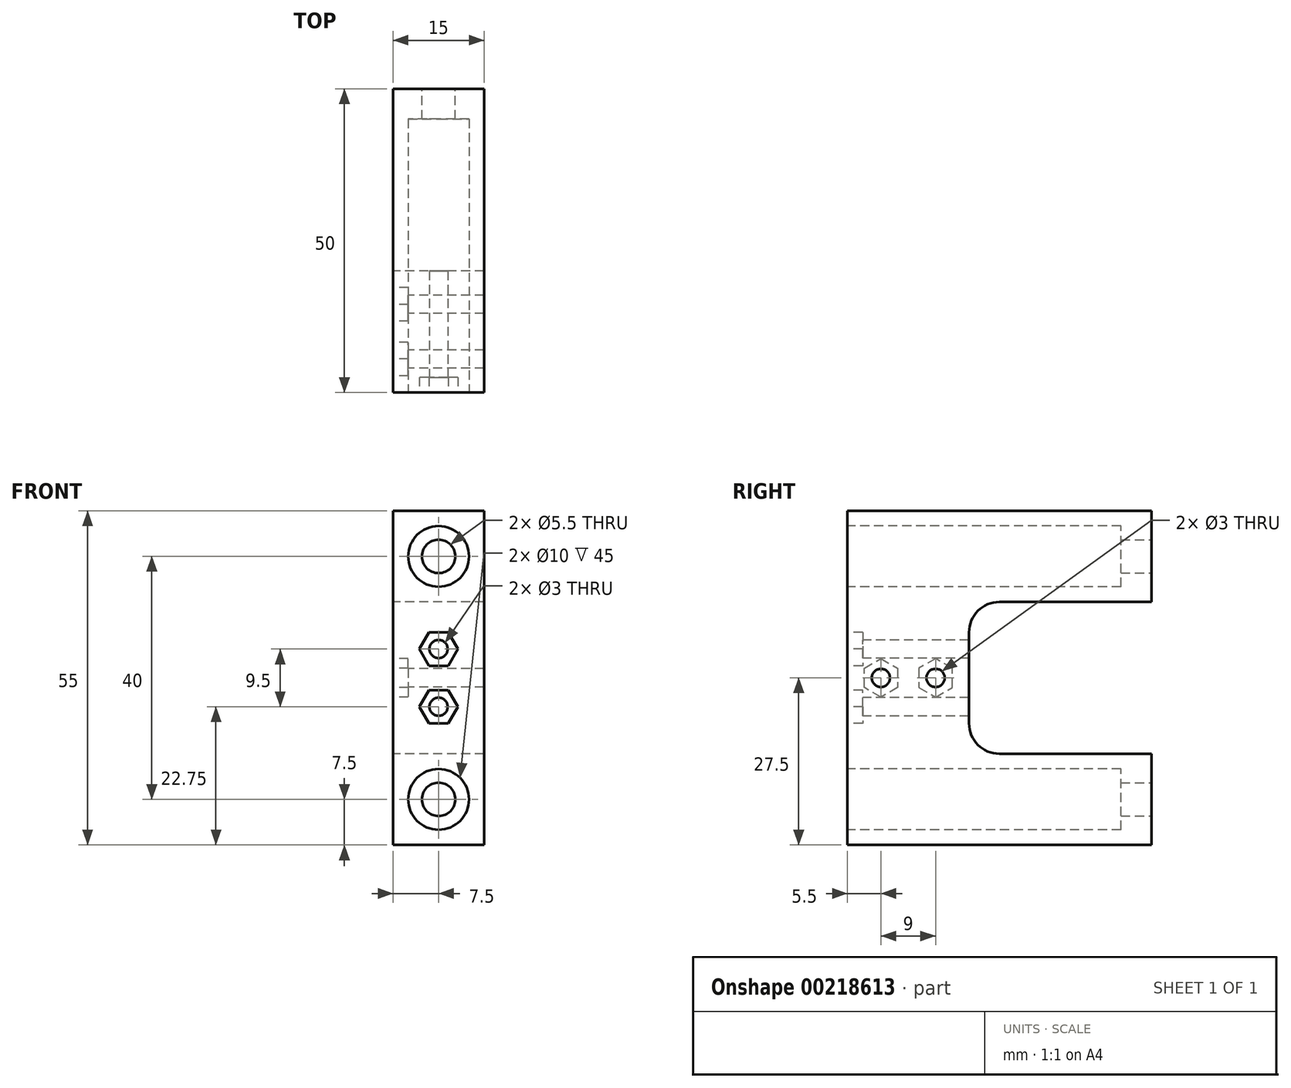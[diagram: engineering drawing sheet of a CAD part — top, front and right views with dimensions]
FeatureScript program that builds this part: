
annotation { "Feature Type Name" : "Feature", "Feature Type Description" : "" }
export const myFeature = defineFeature(function(context is Context, id is Id, definition is map)
    precondition{}
    {
        {
            var Q0;
            Q0=qCreatedBy(makeId("Front.planeOp"),FACE);
            var sketch = newSketch(context, id + "F0", { "sketchPlane" : qUnion([Q0])});
            skLineSegment(sketch, "E0.bottom", {"start": v(7.5, 12.5) * mm, "end": v(-7.5, 12.5) * mm});
            skLineSegment(sketch, "E0.top", {"start": v(7.5, 27.5) * mm, "end": v(-7.5, 27.5) * mm});
            skLineSegment(sketch, "E0.left", {"start": v(7.5, 12.5) * mm, "end": v(7.5, 27.5) * mm});
            skLineSegment(sketch, "E0.right", {"start": v(-7.5, 12.5) * mm, "end": v(-7.5, 27.5) * mm});
            skPoint(sketch, "E0.middle", {"position": v(0, 20) * mm});
            skLineSegment(sketch, "E1", {"start": v(0, 0) * mm, "end": v(34.52, 0) * mm, "construction": true});
            skLineSegment(sketch, "E2.MirrorCS", {"start": v(7.5, -12.5) * mm, "end": v(-7.5, -12.5) * mm});
            skLineSegment(sketch, "E3.MirrorCS", {"start": v(7.5, -12.5) * mm, "end": v(7.5, -27.5) * mm});
            skLineSegment(sketch, "E4.MirrorCS", {"start": v(-7.5, -12.5) * mm, "end": v(-7.5, -27.5) * mm});
            skLineSegment(sketch, "E5.MirrorCS", {"start": v(7.5, -27.5) * mm, "end": v(-7.5, -27.5) * mm});
            skSolve(sketch);
        }
        {
            var Q0;
            Q0 = qSketchRegion(id + "F0", true);
            extrude(context, id + "F1", {"entities" : qUnion([Q0]), "depth" : 50 * mm, "offsetDistance" : 25 * mm});
        }
        {
            var Q0;
            Q0=makeQuery(id+"F1.opExtrude","CAP_FACE",FACE,{"disambiguationData":[OSD([sQuery(id+"F0.wireOp",EDGE,"E0.bottom"),sQuery(id+"F0.wireOp",EDGE,"E0.top"),sQuery(id+"F0.wireOp",EDGE,"E0.left"),sQuery(id+"F0.wireOp",EDGE,"E0.right")])],"isStart":false});
            var sketch = newSketch(context, id + "F2", { "sketchPlane" : qUnion([Q0])});
            skLineSegment(sketch, "E6.bottom", {"start": v(-7.5, 27.5) * mm, "end": v(7.5, 27.5) * mm});
            skLineSegment(sketch, "E6.top", {"start": v(-7.5, -27.5) * mm, "end": v(7.5, -27.5) * mm});
            skLineSegment(sketch, "E6.left", {"start": v(-7.5, 27.5) * mm, "end": v(-7.5, -27.5) * mm});
            skLineSegment(sketch, "E6.right", {"start": v(7.5, 27.5) * mm, "end": v(7.5, -27.5) * mm});
            skSolve(sketch);
        }
        {
            var Q0;
            Q0 = qSketchRegion(id + "F2", true);
            extrude(context, id + "F3", {"entities" : qUnion([Q0]), "operationType" : NewBodyOperationType.ADD, "oppositeDirection" : true, "depth" : 20 * mm, "offsetDistance" : 25 * mm});
        }
        {
            var Q0;
            Q0=makeQuery(id+"F1.opExtrude","CAP_FACE",FACE,{"disambiguationData":[OSD([sQuery(id+"F0.wireOp",EDGE,"E0.bottom"),sQuery(id+"F0.wireOp",EDGE,"E0.top"),sQuery(id+"F0.wireOp",EDGE,"E0.left"),sQuery(id+"F0.wireOp",EDGE,"E0.right")])],"isStart":true});
            var sketch = newSketch(context, id + "F4", { "sketchPlane" : qUnion([Q0])});
            skCircle(sketch, "E7", {"center": v(0, 20) * mm, "radius": 2.75 * mm});
            skPoint(sketch, "E7.centerSnap0", {"position": v(-7.5, 20) * mm});
            skLineSegment(sketch, "E8", {"start": v(0, 0) * mm, "end": v(41.2, 0) * mm, "construction": true});
            skCircle(sketch, "E9.MirrorC", {"center": v(0, -20) * mm, "radius": 2.75 * mm});
            skSolve(sketch);
        }
        {
            var Q0;
            Q0 = qSketchRegion(id + "F4", true);
            extrude(context, id + "F5", {"entities" : qUnion([Q0]), "operationType" : NewBodyOperationType.REMOVE, "endBound" : BoundingType.THROUGH_ALL, "oppositeDirection" : true, "depth" : 25 * mm, "offsetDistance" : 25 * mm});
        }
        {
            var Q0;
            Q0=makeQuery(id+"F3.boolean.opBoolean","MERGE",FACE,{"derivedFrom":[makeQuery(id+"F1.opExtrude","CAP_FACE",FACE,{"disambiguationData":[OSD([sQuery(id+"F0.wireOp",EDGE,"E0.bottom"),sQuery(id+"F0.wireOp",EDGE,"E0.top"),sQuery(id+"F0.wireOp",EDGE,"E0.left"),sQuery(id+"F0.wireOp",EDGE,"E0.right")])],"isStart":false}),makeQuery(id+"F1.opExtrude","CAP_FACE",FACE,{"disambiguationData":[OSD([sQuery(id+"F0.wireOp",EDGE,"E2.MirrorCS"),sQuery(id+"F0.wireOp",EDGE,"E3.MirrorCS"),sQuery(id+"F0.wireOp",EDGE,"E4.MirrorCS"),sQuery(id+"F0.wireOp",EDGE,"E5.MirrorCS")])],"isStart":false}),makeQuery(id+"F3.opExtrude","CAP_FACE",FACE,{"disambiguationData":[OSD([sQuery(id+"F2.wireOp",EDGE,"E6.bottom"),sQuery(id+"F2.wireOp",EDGE,"E6.top"),sQuery(id+"F2.wireOp",EDGE,"E6.left"),sQuery(id+"F2.wireOp",EDGE,"E6.right")])],"isStart":true})]});
            var sketch = newSketch(context, id + "F6", { "sketchPlane" : qUnion([Q0])});
            skCircle(sketch, "E10", {"center": v(0, 20) * mm, "radius": 5 * mm});
            skCircle(sketch, "E11", {"center": v(0, -20) * mm, "radius": 5 * mm});
            skSolve(sketch);
        }
        {
            var Q0;
            Q0 = qSketchRegion(id + "F6", true);
            extrude(context, id + "F7", {"entities" : qUnion([Q0]), "operationType" : NewBodyOperationType.REMOVE, "oppositeDirection" : true, "depth" : 45 * mm, "offsetDistance" : 25 * mm});
        }
        {
            var Q0;
            Q0=makeQuery(id+"F3.boolean.opBoolean","MERGE",FACE,{"derivedFrom":[makeQuery(id+"F1.opExtrude","SWEPT_FACE",FACE,{"disambiguationData":[OSD([sQuery(id+"F0.wireOp",EDGE,"E0.right")])]}),makeQuery(id+"F1.opExtrude","SWEPT_FACE",FACE,{"disambiguationData":[OSD([sQuery(id+"F0.wireOp",EDGE,"E4.MirrorCS")])]}),makeQuery(id+"F3.opExtrude","SWEPT_FACE",FACE,{"disambiguationData":[OSD([sQuery(id+"F2.wireOp",EDGE,"E6.left")])]})]});
            var sketch = newSketch(context, id + "F8", { "sketchPlane" : qUnion([Q0])});
            skCircle(sketch, "E12.cCircle", {"center": v(35.5, 0) * mm, "radius": 2.75 * mm, "construction": true});
            skLineSegment(sketch, "E12.0", {"start": v(38.25, -1.59) * mm, "end": v(35.5, -3.18) * mm});
            skLineSegment(sketch, "E12.1", {"start": v(35.5, -3.18) * mm, "end": v(32.75, -1.59) * mm});
            skLineSegment(sketch, "E12.2", {"start": v(32.75, -1.59) * mm, "end": v(32.75, 1.59) * mm});
            skLineSegment(sketch, "E12.3", {"start": v(32.75, 1.59) * mm, "end": v(35.5, 3.18) * mm});
            skLineSegment(sketch, "E12.4", {"start": v(35.5, 3.18) * mm, "end": v(38.25, 1.59) * mm});
            skLineSegment(sketch, "E12.5", {"start": v(38.25, 1.59) * mm, "end": v(38.25, -1.59) * mm});
            skPoint(sketch, "E12.0.midPoint", {"position": v(36.88, -2.38) * mm});
            skLineSegment(sketch, "E13", {"start": v(30, 0) * mm, "end": v(50, 0) * mm, "construction": true});
            skLineSegment(sketch, "E14", {"start": v(40, 0) * mm, "end": v(40, 5.04) * mm, "construction": true});
            skCircle(sketch, "E15.MirrorC", {"center": v(44.5, 0) * mm, "radius": 2.75 * mm, "construction": true});
            skLineSegment(sketch, "E16.MirrorCS", {"start": v(44.5, 3.18) * mm, "end": v(41.75, 1.59) * mm});
            skLineSegment(sketch, "E17.MirrorCS", {"start": v(41.75, 1.59) * mm, "end": v(41.75, -1.59) * mm});
            skLineSegment(sketch, "E18.MirrorCS", {"start": v(41.75, -1.59) * mm, "end": v(44.5, -3.18) * mm});
            skLineSegment(sketch, "E19.MirrorCS", {"start": v(44.5, -3.18) * mm, "end": v(47.25, -1.59) * mm});
            skLineSegment(sketch, "E20.MirrorCS", {"start": v(47.25, -1.59) * mm, "end": v(47.25, 1.59) * mm});
            skLineSegment(sketch, "E21.MirrorCS", {"start": v(47.25, 1.59) * mm, "end": v(44.5, 3.18) * mm});
            skSolve(sketch);
        }
        {
            var Q0;
            Q0 = qSketchRegion(id + "F8", true);
            extrude(context, id + "F9", {"entities" : qUnion([Q0]), "operationType" : NewBodyOperationType.REMOVE, "oppositeDirection" : true, "depth" : 2.5 * mm, "offsetDistance" : 25 * mm});
        }
        {
            var Q0;
            Q0=makeQuery(id+"F9.boolean.opBoolean","COPY",FACE,{"derivedFrom":makeQuery(id+"F9.opExtrude","CAP_FACE",FACE,{"disambiguationData":[OSD([sQuery(id+"F8.wireOp",EDGE,"E12.0"),sQuery(id+"F8.wireOp",EDGE,"E12.1"),sQuery(id+"F8.wireOp",EDGE,"E12.2"),sQuery(id+"F8.wireOp",EDGE,"E12.3"),sQuery(id+"F8.wireOp",EDGE,"E12.4"),sQuery(id+"F8.wireOp",EDGE,"E12.5")])],"isStart":false})});
            var sketch = newSketch(context, id + "F10", { "sketchPlane" : qUnion([Q0])});
            skCircle(sketch, "E22", {"center": v(35.5, 0) * mm, "radius": 1.5 * mm});
            skCircle(sketch, "E23", {"center": v(44.5, 0) * mm, "radius": 1.5 * mm});
            skSolve(sketch);
        }
        {
            var Q0;
            Q0 = qSketchRegion(id + "F10", true);
            extrude(context, id + "F11", {"entities" : qUnion([Q0]), "operationType" : NewBodyOperationType.REMOVE, "endBound" : BoundingType.THROUGH_ALL, "oppositeDirection" : true, "depth" : 25 * mm, "offsetDistance" : 25 * mm});
        }
        {
            var Q0;
            Q0=makeQuery(id+"F3.boolean.opBoolean","MERGE",FACE,{"derivedFrom":[makeQuery(id+"F1.opExtrude","CAP_FACE",FACE,{"disambiguationData":[OSD([sQuery(id+"F0.wireOp",EDGE,"E0.bottom"),sQuery(id+"F0.wireOp",EDGE,"E0.top"),sQuery(id+"F0.wireOp",EDGE,"E0.left"),sQuery(id+"F0.wireOp",EDGE,"E0.right")])],"isStart":false}),makeQuery(id+"F1.opExtrude","CAP_FACE",FACE,{"disambiguationData":[OSD([sQuery(id+"F0.wireOp",EDGE,"E2.MirrorCS"),sQuery(id+"F0.wireOp",EDGE,"E3.MirrorCS"),sQuery(id+"F0.wireOp",EDGE,"E4.MirrorCS"),sQuery(id+"F0.wireOp",EDGE,"E5.MirrorCS")])],"isStart":false}),makeQuery(id+"F3.opExtrude","CAP_FACE",FACE,{"disambiguationData":[OSD([sQuery(id+"F2.wireOp",EDGE,"E6.bottom"),sQuery(id+"F2.wireOp",EDGE,"E6.top"),sQuery(id+"F2.wireOp",EDGE,"E6.left"),sQuery(id+"F2.wireOp",EDGE,"E6.right")])],"isStart":true})]});
            var sketch = newSketch(context, id + "F12", { "sketchPlane" : qUnion([Q0])});
            skCircle(sketch, "E24.cCircle", {"center": v(0, 4.75) * mm, "radius": 2.75 * mm, "construction": true});
            skLineSegment(sketch, "E24.0", {"start": v(3.18, 4.75) * mm, "end": v(1.59, 2) * mm});
            skLineSegment(sketch, "E24.1", {"start": v(1.59, 2) * mm, "end": v(-1.59, 2) * mm});
            skLineSegment(sketch, "E24.2", {"start": v(-1.59, 2) * mm, "end": v(-3.18, 4.75) * mm});
            skLineSegment(sketch, "E24.3", {"start": v(-3.18, 4.75) * mm, "end": v(-1.59, 7.5) * mm});
            skLineSegment(sketch, "E24.4", {"start": v(-1.59, 7.5) * mm, "end": v(1.59, 7.5) * mm});
            skLineSegment(sketch, "E24.5", {"start": v(1.59, 7.5) * mm, "end": v(3.18, 4.75) * mm});
            skPoint(sketch, "E24.0.midPoint", {"position": v(2.38, 3.37) * mm});
            skLineSegment(sketch, "E25.MirrorCS", {"start": v(3.18, -4.75) * mm, "end": v(1.59, -2) * mm});
            skLineSegment(sketch, "E26.MirrorCS", {"start": v(1.59, -2) * mm, "end": v(-1.59, -2) * mm});
            skLineSegment(sketch, "E27.MirrorCS", {"start": v(-3.18, -4.75) * mm, "end": v(-1.59, -7.5) * mm});
            skLineSegment(sketch, "E28.MirrorCS", {"start": v(-1.59, -2) * mm, "end": v(-3.18, -4.75) * mm});
            skCircle(sketch, "E29.MirrorC", {"center": v(0, -4.75) * mm, "radius": 2.75 * mm, "construction": true});
            skLineSegment(sketch, "E30.MirrorCS", {"start": v(-1.59, -7.5) * mm, "end": v(1.59, -7.5) * mm});
            skLineSegment(sketch, "E31.MirrorCS", {"start": v(1.59, -7.5) * mm, "end": v(3.18, -4.75) * mm});
            skPoint(sketch, "E32.MirrorP", {"position": v(2.38, -3.37) * mm});
            skSolve(sketch);
        }
        {
            var Q0;
            Q0 = qSketchRegion(id + "F12", true);
            extrude(context, id + "F13", {"entities" : qUnion([Q0]), "operationType" : NewBodyOperationType.REMOVE, "oppositeDirection" : true, "depth" : 2.5 * mm, "offsetDistance" : 25 * mm});
        }
        {
            var Q0;
            Q0=makeQuery(id+"F13.boolean.opBoolean","COPY",FACE,{"derivedFrom":makeQuery(id+"F13.opExtrude","CAP_FACE",FACE,{"disambiguationData":[OSD([sQuery(id+"F12.wireOp",EDGE,"E24.0"),sQuery(id+"F12.wireOp",EDGE,"E24.1"),sQuery(id+"F12.wireOp",EDGE,"E24.2"),sQuery(id+"F12.wireOp",EDGE,"E24.3"),sQuery(id+"F12.wireOp",EDGE,"E24.4"),sQuery(id+"F12.wireOp",EDGE,"E24.5")])],"isStart":false})});
            var sketch = newSketch(context, id + "F14", { "sketchPlane" : qUnion([Q0])});
            skCircle(sketch, "E33", {"center": v(0, 4.75) * mm, "radius": 1.5 * mm});
            skCircle(sketch, "E34", {"center": v(0, -4.75) * mm, "radius": 1.5 * mm});
            skSolve(sketch);
        }
        {
            var Q0;
            Q0 = qSketchRegion(id + "F14", true);
            extrude(context, id + "F15", {"entities" : qUnion([Q0]), "operationType" : NewBodyOperationType.REMOVE, "oppositeDirection" : true, "depth" : 25 * mm, "offsetDistance" : 25 * mm});
        }
        {
            var Q0;
            Q0=makeQuery(id+"F3.boolean.opBoolean","INTERSECT",EDGE,{"derivedFrom":[makeQuery(id+"F1.opExtrude","SWEPT_FACE",FACE,{"disambiguationData":[OSD([sQuery(id+"F0.wireOp",EDGE,"E0.bottom")])]}),makeQuery(id+"F3.opExtrude","CAP_FACE",FACE,{"disambiguationData":[OSD([sQuery(id+"F2.wireOp",EDGE,"E6.bottom"),sQuery(id+"F2.wireOp",EDGE,"E6.top"),sQuery(id+"F2.wireOp",EDGE,"E6.left"),sQuery(id+"F2.wireOp",EDGE,"E6.right")])],"isStart":false})]});
            var Q1;
            Q1=makeQuery(id+"F3.boolean.opBoolean","INTERSECT",EDGE,{"derivedFrom":[makeQuery(id+"F1.opExtrude","SWEPT_FACE",FACE,{"disambiguationData":[OSD([sQuery(id+"F0.wireOp",EDGE,"E2.MirrorCS")])]}),makeQuery(id+"F3.opExtrude","CAP_FACE",FACE,{"disambiguationData":[OSD([sQuery(id+"F2.wireOp",EDGE,"E6.bottom"),sQuery(id+"F2.wireOp",EDGE,"E6.top"),sQuery(id+"F2.wireOp",EDGE,"E6.left"),sQuery(id+"F2.wireOp",EDGE,"E6.right")])],"isStart":false})]});
            fillet(context, id + "F16", {"entities" : qUnion([Q0, Q1]), "tangentPropagation" : true, "radius" : 5 * mm, "defaultsChanged" : false, "vertexSettings" : [], "allowEdgeOverflow" : false});
        }
    });
